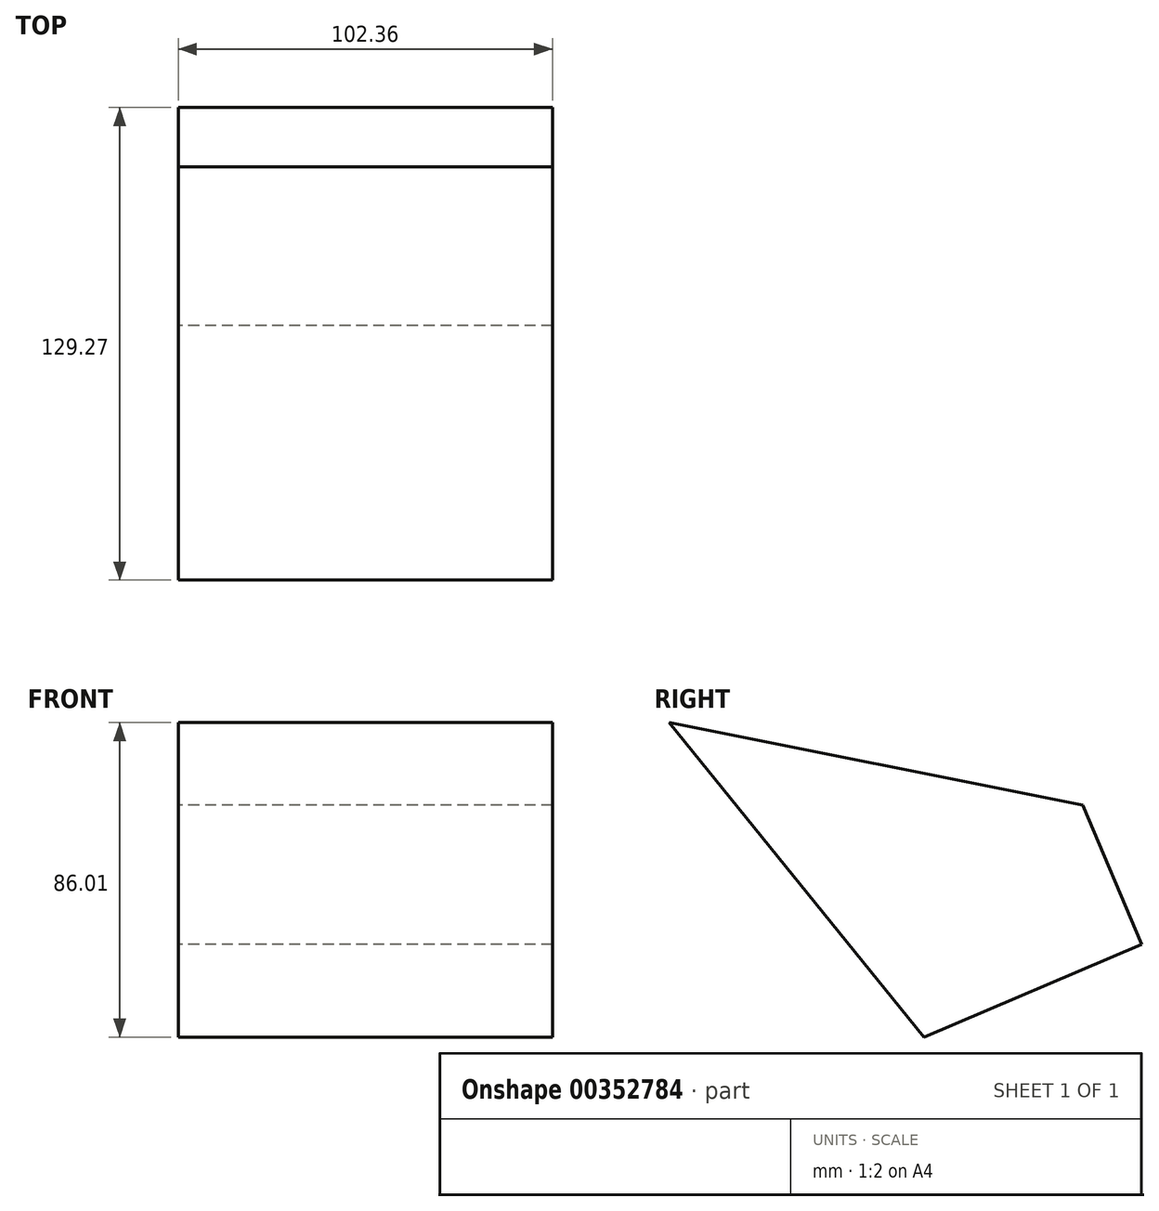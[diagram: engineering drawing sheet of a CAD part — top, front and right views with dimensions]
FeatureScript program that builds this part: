
annotation { "Feature Type Name" : "Feature", "Feature Type Description" : "" }
export const myFeature = defineFeature(function(context is Context, id is Id, definition is map)
    precondition{}
    {
        {
            var Q0;
            Q0=qCreatedBy(makeId("Right.planeOp"),FACE);
            var sketch = newSketch(context, id + "F0", { "sketchPlane" : qUnion([Q0])});
            skLineSegment(sketch, "E0", {"start": v(0, 0) * mm, "end": v(142.71, -28.44) * mm});
            skLineSegment(sketch, "E1", {"start": v(142.71, -28.44) * mm, "end": v(158.9, -66.6) * mm});
            skLineSegment(sketch, "E2", {"start": v(158.9, -66.6) * mm, "end": v(99.24, -91.9) * mm});
            skLineSegment(sketch, "E3", {"start": v(99.24, -91.9) * mm, "end": v(-10.3, 43.43) * mm});
            skLineSegment(sketch, "E4", {"start": v(-10.3, 43.43) * mm, "end": v(0, 0) * mm});
            skSolve(sketch);
        }
        {
            var Q0;
            {var subQ0=sQuery(id+"F0.wireOp",EDGE,"E1");Q0=makeQuery(id+"F0.imprint","IMPRINT",FACE,{"disambiguationData":[TD([[makeQuery(id+"F0.imprint","IMPRINT",EDGE,{"derivedFrom":subQ0}),-1.0]])]});}
            extrude(context, id + "F1", {"entities" : qUnion([Q0]), "depth" : 102.36 * mm});
        }
    });
